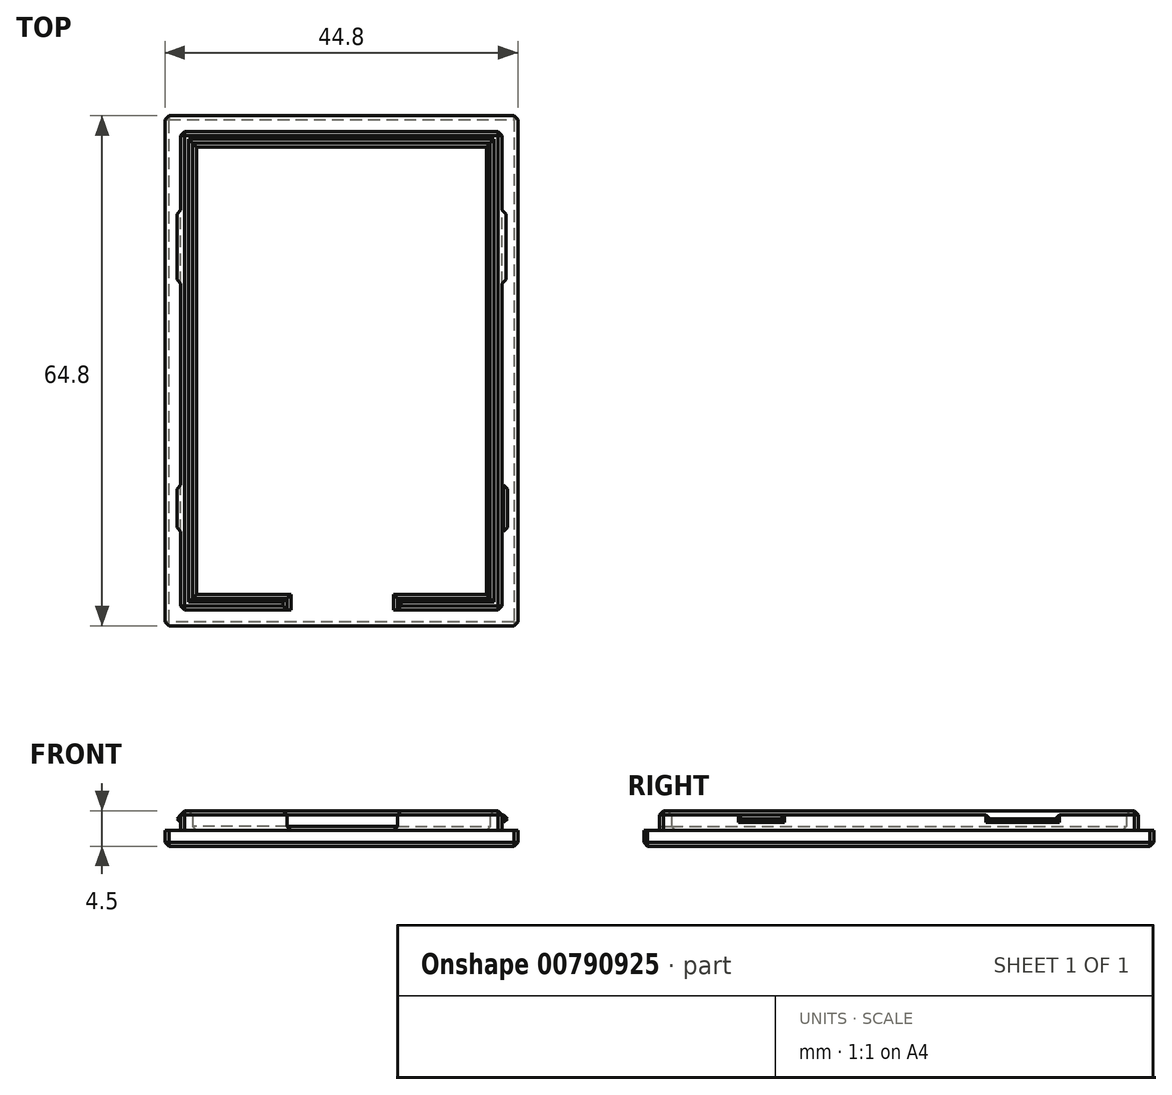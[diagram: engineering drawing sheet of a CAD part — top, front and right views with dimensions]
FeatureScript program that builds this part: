
annotation { "Feature Type Name" : "Feature", "Feature Type Description" : "" }
export const myFeature = defineFeature(function(context is Context, id is Id, definition is map)
    precondition{}
    {
        {
            var Q0;
            Q0=qCreatedBy(makeId("Top.planeOp"),FACE);
            var sketch = newSketch(context, id + "F0", { "sketchPlane" : qUnion([Q0])});
            skLineSegment(sketch, "E0.bottom", {"start": v(-20.5, 35.97) * mm, "end": v(20.3, 35.97) * mm});
            skLineSegment(sketch, "E0.top", {"start": v(-20.5, -24.83) * mm, "end": v(20.3, -24.83) * mm});
            skLineSegment(sketch, "E0.left", {"start": v(-20.5, 35.97) * mm, "end": v(-20.5, -24.83) * mm});
            skLineSegment(sketch, "E0.right", {"start": v(20.3, 35.97) * mm, "end": v(20.3, -24.83) * mm});
            skLineSegment(sketch, "E1.bottom", {"start": v(-22.5, 37.97) * mm, "end": v(22.3, 37.97) * mm});
            skLineSegment(sketch, "E1.top", {"start": v(-22.5, -26.83) * mm, "end": v(22.3, -26.83) * mm});
            skLineSegment(sketch, "E1.left", {"start": v(-22.5, 37.97) * mm, "end": v(-22.5, -26.83) * mm});
            skLineSegment(sketch, "E1.right", {"start": v(22.3, 37.97) * mm, "end": v(22.3, -26.83) * mm});
            skLineSegment(sketch, "E2.bottom", {"start": v(-21, -14.83) * mm, "end": v(21, -14.83) * mm});
            skLineSegment(sketch, "E2.top", {"start": v(-21, -8.96) * mm, "end": v(21, -8.96) * mm});
            skLineSegment(sketch, "E2.left", {"start": v(-21, -14.83) * mm, "end": v(-21, -8.96) * mm});
            skLineSegment(sketch, "E2.right", {"start": v(21, -14.83) * mm, "end": v(21, -8.96) * mm});
            skLineSegment(sketch, "E3.bottom", {"start": v(-21, 16.66) * mm, "end": v(20.8, 16.66) * mm});
            skLineSegment(sketch, "E3.top", {"start": v(-21, 25.97) * mm, "end": v(20.8, 25.97) * mm});
            skLineSegment(sketch, "E3.left", {"start": v(-21, 16.66) * mm, "end": v(-21, 25.97) * mm});
            skLineSegment(sketch, "E3.right", {"start": v(20.8, 16.66) * mm, "end": v(20.8, 25.97) * mm});
            skLineSegment(sketch, "E4.bottom", {"start": v(-17, -29.45) * mm, "end": v(17, -29.45) * mm});
            skLineSegment(sketch, "E4.top", {"start": v(-17, -24.83) * mm, "end": v(17, -24.83) * mm});
            skLineSegment(sketch, "E4.left", {"start": v(-17, -29.45) * mm, "end": v(-17, -24.83) * mm});
            skLineSegment(sketch, "E4.right", {"start": v(17, -29.45) * mm, "end": v(17, -24.83) * mm});
            skLineSegment(sketch, "E5.bottom", {"start": v(-7, -22.91) * mm, "end": v(7, -22.91) * mm});
            skLineSegment(sketch, "E5.top", {"start": v(-7, -32.6) * mm, "end": v(7, -32.6) * mm});
            skLineSegment(sketch, "E5.left", {"start": v(-7, -22.91) * mm, "end": v(-7, -32.6) * mm});
            skLineSegment(sketch, "E5.right", {"start": v(7, -22.91) * mm, "end": v(7, -32.6) * mm});
            skLineSegment(sketch, "E6", {"start": v(22.3, 37.97) * mm, "end": v(27.3, 37.97) * mm});
            skArc(sketch, "E7", {"start": v(27.3, 37.97) * mm, "mid": v(32.3, 32.97) * mm, "end": v(27.3, 27.97) * mm});
            skLineSegment(sketch, "E8", {"start": v(27.3, 27.97) * mm, "end": v(22.3, 25.09) * mm});
            skCircle(sketch, "E9", {"center": v(27.3, 32.97) * mm, "radius": 2.1 * mm});
            skLineSegment(sketch, "E10", {"start": v(-22.5, 37.97) * mm, "end": v(-27.5, 37.97) * mm});
            skArc(sketch, "E11", {"start": v(-27.5, 37.97) * mm, "mid": v(-32.5, 32.97) * mm, "end": v(-27.5, 27.97) * mm});
            skLineSegment(sketch, "E12", {"start": v(-27.5, 27.97) * mm, "end": v(-22.5, 25.09) * mm});
            skLineSegment(sketch, "E13", {"start": v(22.3, -26.83) * mm, "end": v(27.3, -26.83) * mm});
            skArc(sketch, "E14", {"start": v(27.3, -26.83) * mm, "mid": v(32.3, -21.83) * mm, "end": v(27.3, -16.83) * mm});
            skLineSegment(sketch, "E15", {"start": v(27.3, -16.83) * mm, "end": v(22.3, -13.94) * mm});
            skLineSegment(sketch, "E16", {"start": v(-22.5, -26.83) * mm, "end": v(-27.5, -26.83) * mm});
            skArc(sketch, "E17", {"start": v(-27.5, -26.83) * mm, "mid": v(-32.5, -21.83) * mm, "end": v(-27.5, -16.83) * mm});
            skLineSegment(sketch, "E18", {"start": v(-27.5, -16.83) * mm, "end": v(-22.5, -13.94) * mm});
            skCircle(sketch, "E19", {"center": v(-27.5, 32.97) * mm, "radius": 2.1 * mm});
            skCircle(sketch, "E20", {"center": v(-27.5, -21.83) * mm, "radius": 2.1 * mm});
            skCircle(sketch, "E21", {"center": v(27.3, -21.83) * mm, "radius": 2.1 * mm});
            skLineSegment(sketch, "E22.bottom", {"start": v(18.8, 34.47) * mm, "end": v(-19, 34.47) * mm});
            skLineSegment(sketch, "E22.top", {"start": v(18.8, -23.33) * mm, "end": v(-19, -23.33) * mm});
            skLineSegment(sketch, "E22.left", {"start": v(18.8, 34.47) * mm, "end": v(18.8, -23.33) * mm});
            skLineSegment(sketch, "E22.right", {"start": v(-19, 34.47) * mm, "end": v(-19, -23.33) * mm});
            skSolve(sketch);
        }
        {
            var Q0;
            {var subQ29=sQuery(id+"F0.wireOp",EDGE,"E0.bottom");Q0=makeQuery(id+"F0.imprint","IMPRINT",FACE,{"disambiguationData":[TD([[makeQuery(id+"F0.imprint","IMPRINT",EDGE,{"derivedFrom":subQ29}),1.0]])]});}
            var Q1;
            {var subQ29=sQuery(id+"F0.wireOp",EDGE,"E0.bottom");Q1=makeQuery(id+"F0.imprint","IMPRINT",FACE,{"disambiguationData":[TD([[makeQuery(id+"F0.imprint","IMPRINT",EDGE,{"derivedFrom":subQ29}),1.0]])]});}
            var Q2;
            Q2=makeQuery(id+"F0.imprint","IMPRINT",FACE,{"disambiguationData":[TD([[makeQuery(id+"F0.imprint","IMPRINT",EDGE,{"derivedFrom":sQuery(id+"F0.wireOp",EDGE,"677e632e-3eaa-4d09-a5a9-d7e54d0ba1e0")}),-1.0]])]});
            var Q3;
            Q3=makeQuery(id+"F0.imprint","IMPRINT",FACE,{"disambiguationData":[TD([[makeQuery(id+"F0.imprint","IMPRINT",EDGE,{"derivedFrom":sQuery(id+"F0.wireOp",EDGE,"677e632e-3eaa-4d09-a5a9-d7e54d0ba1e0")}),1.0]])]});
            var Q4;
            {var subQ5=sQuery(id+"F0.wireOp",EDGE,"E0.bottom");Q4=makeQuery(id+"F0.imprint","IMPRINT",FACE,{"disambiguationData":[TD([[makeQuery(id+"F0.imprint","IMPRINT",EDGE,{"derivedFrom":subQ5}),-1.0]])]});}
            var Q5;
            Q5=makeQuery(id+"F0.imprint","IMPRINT",FACE,{"disambiguationData":[TD([[makeQuery(id+"F0.imprint","IMPRINT",EDGE,{"derivedFrom":sQuery(id+"F0.wireOp",EDGE,"480dd3ae-46e1-4b28-823d-24966efe9ffa")}),-1.0]])]});
            var Q6;
            Q6=makeQuery(id+"F0.imprint","IMPRINT",FACE,{"disambiguationData":[TD([[makeQuery(id+"F0.imprint","IMPRINT",EDGE,{"derivedFrom":sQuery(id+"F0.wireOp",EDGE,"480dd3ae-46e1-4b28-823d-24966efe9ffa")}),1.0]])]});
            var Q7;
            {var subQ29=sQuery(id+"F0.wireOp",EDGE,"E0.bottom");Q7=makeQuery(id+"F0.imprint","IMPRINT",FACE,{"disambiguationData":[TD([[makeQuery(id+"F0.imprint","IMPRINT",EDGE,{"derivedFrom":subQ29}),1.0]])]});}
            var Q8;
            {var subQ0=sQuery(id+"F0.wireOp",EDGE,"E3.bottom");var subQ1=sQuery(id+"F0.wireOp",EDGE,"E0.left");var subQ2=makeQuery(id+"F0.imprint","INTERSECT",VERTEX,{"derivedFrom":[subQ1,subQ0]});Q8=makeQuery(id+"F0.imprint","IMPRINT",FACE,{"disambiguationData":[TD([[makeQuery(id+"F0.imprint","IMPRINT",EDGE,{"disambiguationData":[TD([[subQ2,1.0]])],"derivedFrom":subQ1}),1.0]])]});}
            var Q9;
            {var subQ0=sQuery(id+"F0.wireOp",EDGE,"E3.bottom");var subQ1=sQuery(id+"F0.wireOp",EDGE,"E0.left");var subQ2=makeQuery(id+"F0.imprint","INTERSECT",VERTEX,{"derivedFrom":[subQ1,subQ0]});Q9=makeQuery(id+"F0.imprint","IMPRINT",FACE,{"disambiguationData":[TD([[makeQuery(id+"F0.imprint","IMPRINT",EDGE,{"disambiguationData":[TD([[subQ2,-1.0]])],"derivedFrom":subQ1}),1.0]])]});}
            var Q10;
            {var subQ3=sQuery(id+"F0.wireOp",EDGE,"1f75b855-5066-40c4-a874-72f5a5b6cba5");var subQ5=sQuery(id+"F0.wireOp",EDGE,"E4.top");var subQ6=makeQuery(id+"F0.imprint","INTERSECT",VERTEX,{"derivedFrom":[subQ3,subQ5]});Q10=makeQuery(id+"F0.imprint","IMPRINT",FACE,{"disambiguationData":[TD([[makeQuery(id+"F0.imprint","IMPRINT",EDGE,{"disambiguationData":[TD([[subQ6,-1.0]])],"derivedFrom":subQ3}),-1.0]])]});}
            var Q11;
            Q11=makeQuery(id+"F0.imprint","IMPRINT",FACE,{"disambiguationData":[TD([[makeQuery(id+"F0.imprint","IMPRINT",EDGE,{"derivedFrom":sQuery(id+"F0.wireOp",EDGE,"79218117-f56a-448c-9f48-c8c58d9f12d9")}),-1.0]])]});
            var Q12;
            {var subQ29=sQuery(id+"F0.wireOp",EDGE,"E0.bottom");Q12=makeQuery(id+"F0.imprint","IMPRINT",FACE,{"disambiguationData":[TD([[makeQuery(id+"F0.imprint","IMPRINT",EDGE,{"derivedFrom":subQ29}),1.0]])]});}
            var Q13;
            {var subQ1=sQuery(id+"F0.wireOp",EDGE,"E5.bottom");Q13=makeQuery(id+"F0.imprint","IMPRINT",FACE,{"disambiguationData":[TD([[makeQuery(id+"F0.imprint","IMPRINT",EDGE,{"derivedFrom":subQ1}),1.0]])]});}
            var Q14;
            {var subQ0=sQuery(id+"F0.wireOp",EDGE,"E2.bottom");var subQ1=sQuery(id+"F0.wireOp",EDGE,"E0.left");var subQ2=makeQuery(id+"F0.imprint","INTERSECT",VERTEX,{"derivedFrom":[subQ1,subQ0]});Q14=makeQuery(id+"F0.imprint","IMPRINT",FACE,{"disambiguationData":[TD([[makeQuery(id+"F0.imprint","IMPRINT",EDGE,{"disambiguationData":[TD([[subQ2,1.0]])],"derivedFrom":subQ1}),1.0]])]});}
            var Q15;
            Q15=makeQuery(id+"F0.imprint","IMPRINT",FACE,{"disambiguationData":[TD([[makeQuery(id+"F0.imprint","IMPRINT",EDGE,{"derivedFrom":sQuery(id+"F0.wireOp",EDGE,"ba33dbd0-b231-4e40-89bf-cbb7f6c2f6bb")}),-1.0]])]});
            var Q16;
            {var subQ0=sQuery(id+"F0.wireOp",EDGE,"E4.left");var subQ3=sQuery(id+"F0.wireOp",EDGE,"849d3ca8-0fda-44a0-b916-5b7dc914c84e");var subQ4=makeQuery(id+"F0.imprint","INTERSECT",VERTEX,{"derivedFrom":[subQ3,subQ0]});Q16=makeQuery(id+"F0.imprint","IMPRINT",FACE,{"disambiguationData":[TD([[makeQuery(id+"F0.imprint","IMPRINT",EDGE,{"disambiguationData":[TD([[subQ4,-1.0]])],"derivedFrom":subQ3}),-1.0]])]});}
            var Q17;
            {var subQ0=sQuery(id+"F0.wireOp",EDGE,"E5.left");var subQ1=sQuery(id+"F0.wireOp",EDGE,"E0.top");var subQ2=makeQuery(id+"F0.imprint","INTERSECT",VERTEX,{"derivedFrom":[subQ1,subQ0]});Q17=makeQuery(id+"F0.imprint","IMPRINT",FACE,{"disambiguationData":[TD([[makeQuery(id+"F0.imprint","IMPRINT",EDGE,{"disambiguationData":[TD([[subQ2,-1.0]])],"derivedFrom":subQ1}),-1.0]])]});}
            var Q18;
            {var subQ0=sQuery(id+"F0.wireOp",EDGE,"E5.bottom");Q18=makeQuery(id+"F0.imprint","IMPRINT",FACE,{"disambiguationData":[TD([[makeQuery(id+"F0.imprint","IMPRINT",EDGE,{"derivedFrom":subQ0}),-1.0]])]});}
            var Q19;
            Q19=makeQuery(id+"F0.imprint","IMPRINT",FACE,{"disambiguationData":[TD([[makeQuery(id+"F0.imprint","IMPRINT",EDGE,{"derivedFrom":sQuery(id+"F0.wireOp",EDGE,"ba33dbd0-b231-4e40-89bf-cbb7f6c2f6bb")}),1.0]])]});
            var Q20;
            {var subQ29=sQuery(id+"F0.wireOp",EDGE,"E0.bottom");Q20=makeQuery(id+"F0.imprint","IMPRINT",FACE,{"disambiguationData":[TD([[makeQuery(id+"F0.imprint","IMPRINT",EDGE,{"derivedFrom":subQ29}),1.0]])]});}
            var Q21;
            {var subQ1=sQuery(id+"F0.wireOp",EDGE,"E0.top");var subQ3=sQuery(id+"F0.wireOp",EDGE,"849d3ca8-0fda-44a0-b916-5b7dc914c84e");var subQ4=makeQuery(id+"F0.imprint","INTERSECT",VERTEX,{"derivedFrom":[subQ1,subQ3]});Q21=makeQuery(id+"F0.imprint","IMPRINT",FACE,{"disambiguationData":[TD([[makeQuery(id+"F0.imprint","IMPRINT",EDGE,{"disambiguationData":[TD([[subQ4,-1.0]])],"derivedFrom":subQ3}),1.0]])]});}
            var Q22;
            {var subQ5=sQuery(id+"F0.wireOp",EDGE,"E0.top");var subQ8=sQuery(id+"F0.wireOp",EDGE,"E5.left");var subQ9=makeQuery(id+"F0.imprint","INTERSECT",VERTEX,{"derivedFrom":[subQ5,subQ8]});Q22=makeQuery(id+"F0.imprint","IMPRINT",FACE,{"disambiguationData":[TD([[makeQuery(id+"F0.imprint","IMPRINT",EDGE,{"disambiguationData":[TD([[subQ9,1.0]])],"derivedFrom":subQ5}),1.0]])]});}
            var Q23;
            {var subQ0=sQuery(id+"F0.wireOp",EDGE,"E4.left");var subQ1=sQuery(id+"F0.wireOp",EDGE,"849d3ca8-0fda-44a0-b916-5b7dc914c84e");var subQ2=makeQuery(id+"F0.imprint","INTERSECT",VERTEX,{"derivedFrom":[subQ1,subQ0]});Q23=makeQuery(id+"F0.imprint","IMPRINT",FACE,{"disambiguationData":[TD([[makeQuery(id+"F0.imprint","IMPRINT",EDGE,{"disambiguationData":[TD([[subQ2,-1.0]])],"derivedFrom":subQ1}),1.0]])]});}
            var Q24;
            {var subQ0=sQuery(id+"F0.wireOp",EDGE,"E4.top");var subQ1=sQuery(id+"F0.wireOp",EDGE,"1f75b855-5066-40c4-a874-72f5a5b6cba5");var subQ2=makeQuery(id+"F0.imprint","INTERSECT",VERTEX,{"derivedFrom":[subQ1,subQ0]});Q24=makeQuery(id+"F0.imprint","IMPRINT",FACE,{"disambiguationData":[TD([[makeQuery(id+"F0.imprint","IMPRINT",EDGE,{"disambiguationData":[TD([[subQ2,-1.0]])],"derivedFrom":subQ1}),1.0]])]});}
            var Q25;
            {var subQ0=sQuery(id+"F0.wireOp",EDGE,"1f75b855-5066-40c4-a874-72f5a5b6cba5");var subQ3=sQuery(id+"F0.wireOp",EDGE,"E4.right");var subQ5=makeQuery(id+"F0.imprint","INTERSECT",VERTEX,{"derivedFrom":[subQ0,subQ3]});Q25=makeQuery(id+"F0.imprint","IMPRINT",FACE,{"disambiguationData":[TD([[makeQuery(id+"F0.imprint","IMPRINT",EDGE,{"disambiguationData":[TD([[subQ5,-1.0]])],"derivedFrom":subQ0}),1.0]])]});}
            var Q26;
            Q26=makeQuery(id+"F0.imprint","IMPRINT",FACE,{"disambiguationData":[TD([[makeQuery(id+"F0.imprint","IMPRINT",EDGE,{"derivedFrom":sQuery(id+"F0.wireOp",EDGE,"79218117-f56a-448c-9f48-c8c58d9f12d9")}),1.0]])]});
            var Q27;
            {var subQ5=sQuery(id+"F0.wireOp",EDGE,"E2.right");Q27=makeQuery(id+"F0.imprint","IMPRINT",FACE,{"disambiguationData":[TD([[makeQuery(id+"F0.imprint","IMPRINT",EDGE,{"derivedFrom":subQ5}),1.0]])]});}
            var Q28;
            {var subQ5=sQuery(id+"F0.wireOp",EDGE,"E2.left");Q28=makeQuery(id+"F0.imprint","IMPRINT",FACE,{"disambiguationData":[TD([[makeQuery(id+"F0.imprint","IMPRINT",EDGE,{"derivedFrom":subQ5}),-1.0]])]});}
            var Q29;
            {var subQ5=sQuery(id+"F0.wireOp",EDGE,"E3.left");Q29=makeQuery(id+"F0.imprint","IMPRINT",FACE,{"disambiguationData":[TD([[makeQuery(id+"F0.imprint","IMPRINT",EDGE,{"derivedFrom":subQ5}),-1.0]])]});}
            var Q30;
            {var subQ5=sQuery(id+"F0.wireOp",EDGE,"E3.right");Q30=makeQuery(id+"F0.imprint","IMPRINT",FACE,{"disambiguationData":[TD([[makeQuery(id+"F0.imprint","IMPRINT",EDGE,{"derivedFrom":subQ5}),1.0]])]});}
            var Q31;
            {var subQ5=sQuery(id+"F0.wireOp",EDGE,"E22.bottom");Q31=makeQuery(id+"F0.imprint","IMPRINT",FACE,{"disambiguationData":[TD([[makeQuery(id+"F0.imprint","IMPRINT",EDGE,{"derivedFrom":subQ5}),1.0]])]});}
            var Q32;
            {var subQ0=sQuery(id+"F0.wireOp",EDGE,"E22.right");var subQ1=sQuery(id+"F0.wireOp",EDGE,"E3.bottom");var subQ2=makeQuery(id+"F0.imprint","INTERSECT",VERTEX,{"derivedFrom":[subQ1,subQ0]});Q32=makeQuery(id+"F0.imprint","IMPRINT",FACE,{"disambiguationData":[TD([[makeQuery(id+"F0.imprint","IMPRINT",EDGE,{"disambiguationData":[TD([[subQ2,-1.0]])],"derivedFrom":subQ1}),1.0]])]});}
            var Q33;
            {var subQ0=sQuery(id+"F0.wireOp",EDGE,"E22.right");var subQ1=sQuery(id+"F0.wireOp",EDGE,"E2.top");var subQ2=makeQuery(id+"F0.imprint","INTERSECT",VERTEX,{"derivedFrom":[subQ1,subQ0]});Q33=makeQuery(id+"F0.imprint","IMPRINT",FACE,{"disambiguationData":[TD([[makeQuery(id+"F0.imprint","IMPRINT",EDGE,{"disambiguationData":[TD([[subQ2,-1.0]])],"derivedFrom":subQ1}),1.0]])]});}
            var Q34;
            {var subQ0=sQuery(id+"F0.wireOp",EDGE,"E22.right");var subQ1=sQuery(id+"F0.wireOp",EDGE,"E2.bottom");var subQ2=makeQuery(id+"F0.imprint","INTERSECT",VERTEX,{"derivedFrom":[subQ1,subQ0]});Q34=makeQuery(id+"F0.imprint","IMPRINT",FACE,{"disambiguationData":[TD([[makeQuery(id+"F0.imprint","IMPRINT",EDGE,{"disambiguationData":[TD([[subQ2,-1.0]])],"derivedFrom":subQ1}),1.0]])]});}
            var Q35;
            {var subQ0=sQuery(id+"F0.wireOp",EDGE,"E5.left");var subQ1=sQuery(id+"F0.wireOp",EDGE,"E0.top");var subQ2=makeQuery(id+"F0.imprint","INTERSECT",VERTEX,{"derivedFrom":[subQ1,subQ0]});Q35=makeQuery(id+"F0.imprint","IMPRINT",FACE,{"disambiguationData":[TD([[makeQuery(id+"F0.imprint","IMPRINT",EDGE,{"disambiguationData":[TD([[subQ2,1.0]])],"derivedFrom":subQ1}),-1.0]])]});}
            var Q36;
            {var subQ0=sQuery(id+"F0.wireOp",EDGE,"E5.left");var subQ1=sQuery(id+"F0.wireOp",EDGE,"E0.top");var subQ2=makeQuery(id+"F0.imprint","INTERSECT",VERTEX,{"derivedFrom":[subQ1,subQ0]});Q36=makeQuery(id+"F0.imprint","IMPRINT",FACE,{"disambiguationData":[TD([[makeQuery(id+"F0.imprint","IMPRINT",EDGE,{"disambiguationData":[TD([[subQ2,-1.0]])],"derivedFrom":subQ1}),1.0]])]});}
            var Q37;
            {var subQ5=sQuery(id+"F0.wireOp",EDGE,"E0.top");var subQ7=makeQuery(id+"F0.imprint","INTERSECT",VERTEX,{"derivedFrom":[subQ5,sQuery(id+"F0.wireOp",EDGE,"E4.right")]});Q37=makeQuery(id+"F0.imprint","IMPRINT",FACE,{"disambiguationData":[TD([[makeQuery(id+"F0.imprint","IMPRINT",EDGE,{"disambiguationData":[TD([[subQ7,1.0]])],"derivedFrom":subQ5}),1.0]])]});}
            var Q38;
            {var subQ0=sQuery(id+"F0.wireOp",EDGE,"E4.right");var subQ1=sQuery(id+"F0.wireOp",EDGE,"E0.top");var subQ2=makeQuery(id+"F0.imprint","INTERSECT",VERTEX,{"derivedFrom":[subQ1,subQ0]});Q38=makeQuery(id+"F0.imprint","IMPRINT",FACE,{"disambiguationData":[TD([[makeQuery(id+"F0.imprint","IMPRINT",EDGE,{"disambiguationData":[TD([[subQ2,1.0]])],"derivedFrom":subQ1}),-1.0]])]});}
            var Q39;
            {var subQ0=sQuery(id+"F0.wireOp",EDGE,"E2.bottom");var subQ1=sQuery(id+"F0.wireOp",EDGE,"E0.right");var subQ2=makeQuery(id+"F0.imprint","INTERSECT",VERTEX,{"derivedFrom":[subQ1,subQ0]});Q39=makeQuery(id+"F0.imprint","IMPRINT",FACE,{"disambiguationData":[TD([[makeQuery(id+"F0.imprint","IMPRINT",EDGE,{"disambiguationData":[TD([[subQ2,1.0]])],"derivedFrom":subQ1}),-1.0]])]});}
            var Q40;
            {var subQ0=sQuery(id+"F0.wireOp",EDGE,"E3.bottom");var subQ1=sQuery(id+"F0.wireOp",EDGE,"E0.right");var subQ2=makeQuery(id+"F0.imprint","INTERSECT",VERTEX,{"derivedFrom":[subQ1,subQ0]});Q40=makeQuery(id+"F0.imprint","IMPRINT",FACE,{"disambiguationData":[TD([[makeQuery(id+"F0.imprint","IMPRINT",EDGE,{"disambiguationData":[TD([[subQ2,-1.0]])],"derivedFrom":subQ1}),-1.0]])]});}
            var Q41;
            {var subQ0=sQuery(id+"F0.wireOp",EDGE,"E3.bottom");var subQ1=sQuery(id+"F0.wireOp",EDGE,"E0.right");var subQ2=makeQuery(id+"F0.imprint","INTERSECT",VERTEX,{"derivedFrom":[subQ1,subQ0]});Q41=makeQuery(id+"F0.imprint","IMPRINT",FACE,{"disambiguationData":[TD([[makeQuery(id+"F0.imprint","IMPRINT",EDGE,{"disambiguationData":[TD([[subQ2,1.0]])],"derivedFrom":subQ1}),-1.0]])]});}
            extrude(context, id + "F1", {"entities" : qUnion([Q0, Q1, Q2, Q3, Q4, Q5, Q6, Q7, Q8, Q9, Q10, Q11, Q12, Q13, Q14, Q15, Q16, Q17, Q18, Q19, Q20, Q21, Q22, Q23, Q24, Q25, Q26, Q27, Q28, Q29, Q30, Q31, Q32, Q33, Q34, Q35, Q36, Q37, Q38, Q39, Q40, Q41]), "depth" : 2 * mm, "offsetDistance" : 25 * mm});
        }
        {
            var Q0;
            {var subQ5=sQuery(id+"F0.wireOp",EDGE,"E0.bottom");Q0=makeQuery(id+"F0.imprint","IMPRINT",FACE,{"disambiguationData":[TD([[makeQuery(id+"F0.imprint","IMPRINT",EDGE,{"derivedFrom":subQ5}),-1.0]])]});}
            var Q1;
            {var subQ0=sQuery(id+"F0.wireOp",EDGE,"E3.bottom");var subQ1=sQuery(id+"F0.wireOp",EDGE,"E0.left");var subQ2=makeQuery(id+"F0.imprint","INTERSECT",VERTEX,{"derivedFrom":[subQ1,subQ0]});Q1=makeQuery(id+"F0.imprint","IMPRINT",FACE,{"disambiguationData":[TD([[makeQuery(id+"F0.imprint","IMPRINT",EDGE,{"disambiguationData":[TD([[subQ2,1.0]])],"derivedFrom":subQ1}),1.0]])]});}
            var Q2;
            {var subQ0=sQuery(id+"F0.wireOp",EDGE,"E3.bottom");var subQ1=sQuery(id+"F0.wireOp",EDGE,"E0.left");var subQ2=makeQuery(id+"F0.imprint","INTERSECT",VERTEX,{"derivedFrom":[subQ1,subQ0]});Q2=makeQuery(id+"F0.imprint","IMPRINT",FACE,{"disambiguationData":[TD([[makeQuery(id+"F0.imprint","IMPRINT",EDGE,{"disambiguationData":[TD([[subQ2,-1.0]])],"derivedFrom":subQ1}),1.0]])]});}
            var Q3;
            {var subQ0=sQuery(id+"F0.wireOp",EDGE,"E3.bottom");var subQ1=sQuery(id+"F0.wireOp",EDGE,"E0.right");var subQ2=makeQuery(id+"F0.imprint","INTERSECT",VERTEX,{"derivedFrom":[subQ1,subQ0]});Q3=makeQuery(id+"F0.imprint","IMPRINT",FACE,{"disambiguationData":[TD([[makeQuery(id+"F0.imprint","IMPRINT",EDGE,{"disambiguationData":[TD([[subQ2,1.0]])],"derivedFrom":subQ1}),-1.0]])]});}
            var Q4;
            {var subQ0=sQuery(id+"F0.wireOp",EDGE,"E3.bottom");var subQ1=sQuery(id+"F0.wireOp",EDGE,"E0.right");var subQ2=makeQuery(id+"F0.imprint","INTERSECT",VERTEX,{"derivedFrom":[subQ1,subQ0]});Q4=makeQuery(id+"F0.imprint","IMPRINT",FACE,{"disambiguationData":[TD([[makeQuery(id+"F0.imprint","IMPRINT",EDGE,{"disambiguationData":[TD([[subQ2,-1.0]])],"derivedFrom":subQ1}),-1.0]])]});}
            var Q5;
            {var subQ5=sQuery(id+"F0.wireOp",EDGE,"E0.top");var subQ7=makeQuery(id+"F0.imprint","INTERSECT",VERTEX,{"derivedFrom":[subQ5,sQuery(id+"F0.wireOp",EDGE,"E4.right")]});Q5=makeQuery(id+"F0.imprint","IMPRINT",FACE,{"disambiguationData":[TD([[makeQuery(id+"F0.imprint","IMPRINT",EDGE,{"disambiguationData":[TD([[subQ7,1.0]])],"derivedFrom":subQ5}),1.0]])]});}
            var Q6;
            {var subQ0=sQuery(id+"F0.wireOp",EDGE,"E2.bottom");var subQ1=sQuery(id+"F0.wireOp",EDGE,"E0.right");var subQ2=makeQuery(id+"F0.imprint","INTERSECT",VERTEX,{"derivedFrom":[subQ1,subQ0]});Q6=makeQuery(id+"F0.imprint","IMPRINT",FACE,{"disambiguationData":[TD([[makeQuery(id+"F0.imprint","IMPRINT",EDGE,{"disambiguationData":[TD([[subQ2,1.0]])],"derivedFrom":subQ1}),-1.0]])]});}
            var Q7;
            {var subQ5=sQuery(id+"F0.wireOp",EDGE,"E0.top");var subQ8=sQuery(id+"F0.wireOp",EDGE,"E5.left");var subQ9=makeQuery(id+"F0.imprint","INTERSECT",VERTEX,{"derivedFrom":[subQ5,subQ8]});Q7=makeQuery(id+"F0.imprint","IMPRINT",FACE,{"disambiguationData":[TD([[makeQuery(id+"F0.imprint","IMPRINT",EDGE,{"disambiguationData":[TD([[subQ9,1.0]])],"derivedFrom":subQ5}),1.0]])]});}
            var Q8;
            {var subQ0=sQuery(id+"F0.wireOp",EDGE,"E2.bottom");var subQ1=sQuery(id+"F0.wireOp",EDGE,"E0.left");var subQ2=makeQuery(id+"F0.imprint","INTERSECT",VERTEX,{"derivedFrom":[subQ1,subQ0]});Q8=makeQuery(id+"F0.imprint","IMPRINT",FACE,{"disambiguationData":[TD([[makeQuery(id+"F0.imprint","IMPRINT",EDGE,{"disambiguationData":[TD([[subQ2,1.0]])],"derivedFrom":subQ1}),1.0]])]});}
            extrude(context, id + "F2", {"entities" : qUnion([Q0, Q1, Q2, Q3, Q4, Q5, Q6, Q7, Q8]), "operationType" : NewBodyOperationType.ADD, "depth" : 4.5 * mm, "offsetDistance" : 25 * mm, "hasSecondDirection" : true, "secondDirectionOppositeDirection" : false, "secondDirectionDepth" : 1 * mm});
        }
        {
            var Q0;
            {var subQ5=sQuery(id+"F0.wireOp",EDGE,"E3.right");Q0=makeQuery(id+"F0.imprint","IMPRINT",FACE,{"disambiguationData":[TD([[makeQuery(id+"F0.imprint","IMPRINT",EDGE,{"derivedFrom":subQ5}),1.0]])]});}
            var Q1;
            {var subQ5=sQuery(id+"F0.wireOp",EDGE,"E3.left");Q1=makeQuery(id+"F0.imprint","IMPRINT",FACE,{"disambiguationData":[TD([[makeQuery(id+"F0.imprint","IMPRINT",EDGE,{"derivedFrom":subQ5}),-1.0]])]});}
            var Q2;
            {var subQ5=sQuery(id+"F0.wireOp",EDGE,"E2.left");Q2=makeQuery(id+"F0.imprint","IMPRINT",FACE,{"disambiguationData":[TD([[makeQuery(id+"F0.imprint","IMPRINT",EDGE,{"derivedFrom":subQ5}),-1.0]])]});}
            var Q3;
            {var subQ5=sQuery(id+"F0.wireOp",EDGE,"E2.right");Q3=makeQuery(id+"F0.imprint","IMPRINT",FACE,{"disambiguationData":[TD([[makeQuery(id+"F0.imprint","IMPRINT",EDGE,{"derivedFrom":subQ5}),1.0]])]});}
            extrude(context, id + "F3", {"entities" : qUnion([Q0, Q1, Q2, Q3]), "operationType" : NewBodyOperationType.ADD, "depth" : 4 * mm, "offsetDistance" : 25 * mm, "hasSecondDirection" : true, "secondDirectionOppositeDirection" : false, "secondDirectionDepth" : 3 * mm});
        }
        {
            var Q0;
            Q0=makeQuery(id+"F3.opExtrude","SWEPT_FACE",FACE,{"disambiguationData":[OSD([sQuery(id+"F0.wireOp",EDGE,"E3.left")])]});
            var Q1;
            Q1=makeQuery(id+"F3.opExtrude","SWEPT_FACE",FACE,{"disambiguationData":[OSD([sQuery(id+"F0.wireOp",EDGE,"E2.left")])]});
            var Q2;
            Q2=makeQuery(id+"F3.opExtrude","SWEPT_FACE",FACE,{"disambiguationData":[OSD([sQuery(id+"F0.wireOp",EDGE,"E3.right")])]});
            var Q3;
            Q3=makeQuery(id+"F3.opExtrude","SWEPT_FACE",FACE,{"disambiguationData":[OSD([sQuery(id+"F0.wireOp",EDGE,"E2.right")])]});
            var Q4;
            Q4=makeQuery(id+"F2.opExtrude","SWEPT_EDGE",EDGE,{"disambiguationData":[OSD([sQuery(id+"F0.wireOp",EDGE,"E0.top"),sQuery(id+"F0.wireOp",EDGE,"E0.right")])]});
            var Q5;
            Q5=makeQuery(id+"F2.opExtrude","SWEPT_EDGE",EDGE,{"disambiguationData":[OSD([sQuery(id+"F0.wireOp",EDGE,"E0.bottom"),sQuery(id+"F0.wireOp",EDGE,"E0.right")])]});
            var Q6;
            Q6=makeQuery(id+"F2.opExtrude","CAP_FACE",FACE,{"disambiguationData":[OSD([sQuery(id+"F0.wireOp",EDGE,"E0.bottom"),sQuery(id+"F0.wireOp",EDGE,"E0.top"),sQuery(id+"F0.wireOp",EDGE,"E0.left"),sQuery(id+"F0.wireOp",EDGE,"E0.right"),sQuery(id+"F0.wireOp",EDGE,"E5.left"),sQuery(id+"F0.wireOp",EDGE,"E5.right"),sQuery(id+"F0.wireOp",EDGE,"E22.bottom"),sQuery(id+"F0.wireOp",EDGE,"E22.top"),sQuery(id+"F0.wireOp",EDGE,"E22.left"),sQuery(id+"F0.wireOp",EDGE,"E22.right")])],"isStart":false});
            var Q7;
            Q7=makeQuery(id+"F2.opExtrude","SWEPT_EDGE",EDGE,{"disambiguationData":[OSD([sQuery(id+"F0.wireOp",EDGE,"E0.bottom"),sQuery(id+"F0.wireOp",EDGE,"E0.left")])]});
            var Q8;
            Q8=makeQuery(id+"F1.opExtrude","SWEPT_EDGE",EDGE,{"disambiguationData":[OSD([sQuery(id+"F0.wireOp",EDGE,"E1.bottom"),sQuery(id+"F0.wireOp",EDGE,"E1.left"),sQuery(id+"F0.wireOp",EDGE,"E10")])]});
            var Q9;
            Q9=makeQuery(id+"F2.opExtrude","SWEPT_EDGE",EDGE,{"disambiguationData":[OSD([sQuery(id+"F0.wireOp",EDGE,"E0.top"),sQuery(id+"F0.wireOp",EDGE,"E0.left")])]});
            var Q10;
            Q10=makeQuery(id+"F1.opExtrude","SWEPT_EDGE",EDGE,{"disambiguationData":[OSD([sQuery(id+"F0.wireOp",EDGE,"E1.top"),sQuery(id+"F0.wireOp",EDGE,"E1.left"),sQuery(id+"F0.wireOp",EDGE,"E16")])]});
            var Q11;
            Q11=makeQuery(id+"F1.opExtrude","SWEPT_EDGE",EDGE,{"disambiguationData":[OSD([sQuery(id+"F0.wireOp",EDGE,"E1.top"),sQuery(id+"F0.wireOp",EDGE,"E1.right"),sQuery(id+"F0.wireOp",EDGE,"E13")])]});
            var Q12;
            Q12=makeQuery(id+"F1.opExtrude","CAP_FACE",FACE,{"disambiguationData":[OSD([sQuery(id+"F0.wireOp",EDGE,"E1.bottom"),sQuery(id+"F0.wireOp",EDGE,"E1.top"),sQuery(id+"F0.wireOp",EDGE,"E1.left"),sQuery(id+"F0.wireOp",EDGE,"E1.right")])],"isStart":true});
            var Q13;
            {var subQ0=sQuery(id+"F0.wireOp",EDGE,"E22.top");Q13=makeQuery(id+"F2.boolean.opBoolean","INTERSECT",EDGE,{"derivedFrom":[makeQuery(id+"F1.opExtrude","CAP_FACE",FACE,{"disambiguationData":[OSD([sQuery(id+"F0.wireOp",EDGE,"E1.bottom"),sQuery(id+"F0.wireOp",EDGE,"E1.top"),sQuery(id+"F0.wireOp",EDGE,"E1.left"),sQuery(id+"F0.wireOp",EDGE,"E1.right")])],"isStart":false}),makeQuery(id+"F2.opExtrude","SWEPT_FACE",FACE,{"disambiguationData":[OSD([subQ0]),TDD([makeQuery(id+"F0.imprint","IMPRINT",EDGE,{"disambiguationData":[TD([[makeQuery(id+"F0.imprint","INTERSECT",VERTEX,{"derivedFrom":[sQuery(id+"F0.wireOp",EDGE,"E5.right"),subQ0]}),1.0]])],"derivedFrom":subQ0})])]})]});}
            var Q14;
            Q14=makeQuery(id+"F2.boolean.opBoolean","INTERSECT",EDGE,{"derivedFrom":[makeQuery(id+"F1.opExtrude","CAP_FACE",FACE,{"disambiguationData":[OSD([sQuery(id+"F0.wireOp",EDGE,"E1.bottom"),sQuery(id+"F0.wireOp",EDGE,"E1.top"),sQuery(id+"F0.wireOp",EDGE,"E1.left"),sQuery(id+"F0.wireOp",EDGE,"E1.right")])],"isStart":false}),makeQuery(id+"F2.opExtrude","SWEPT_FACE",FACE,{"disambiguationData":[OSD([sQuery(id+"F0.wireOp",EDGE,"E22.left")])]})]});
            var Q15;
            {var subQ0=sQuery(id+"F0.wireOp",EDGE,"E22.top");Q15=makeQuery(id+"F2.boolean.opBoolean","INTERSECT",EDGE,{"derivedFrom":[makeQuery(id+"F1.opExtrude","CAP_FACE",FACE,{"disambiguationData":[OSD([sQuery(id+"F0.wireOp",EDGE,"E1.bottom"),sQuery(id+"F0.wireOp",EDGE,"E1.top"),sQuery(id+"F0.wireOp",EDGE,"E1.left"),sQuery(id+"F0.wireOp",EDGE,"E1.right")])],"isStart":false}),makeQuery(id+"F2.opExtrude","SWEPT_FACE",FACE,{"disambiguationData":[OSD([subQ0]),TDD([makeQuery(id+"F0.imprint","IMPRINT",EDGE,{"disambiguationData":[TD([[makeQuery(id+"F0.imprint","INTERSECT",VERTEX,{"derivedFrom":[sQuery(id+"F0.wireOp",EDGE,"E5.left"),subQ0]}),-1.0]])],"derivedFrom":subQ0})])]})]});}
            var Q16;
            Q16=makeQuery(id+"F2.boolean.opBoolean","INTERSECT",EDGE,{"derivedFrom":[makeQuery(id+"F1.opExtrude","CAP_FACE",FACE,{"disambiguationData":[OSD([sQuery(id+"F0.wireOp",EDGE,"E1.bottom"),sQuery(id+"F0.wireOp",EDGE,"E1.top"),sQuery(id+"F0.wireOp",EDGE,"E1.left"),sQuery(id+"F0.wireOp",EDGE,"E1.right")])],"isStart":false}),makeQuery(id+"F2.opExtrude","SWEPT_FACE",FACE,{"disambiguationData":[OSD([sQuery(id+"F0.wireOp",EDGE,"E22.right")])]})]});
            var Q17;
            Q17=makeQuery(id+"F2.boolean.opBoolean","INTERSECT",EDGE,{"derivedFrom":[makeQuery(id+"F1.opExtrude","CAP_FACE",FACE,{"disambiguationData":[OSD([sQuery(id+"F0.wireOp",EDGE,"E1.bottom"),sQuery(id+"F0.wireOp",EDGE,"E1.top"),sQuery(id+"F0.wireOp",EDGE,"E1.left"),sQuery(id+"F0.wireOp",EDGE,"E1.right")])],"isStart":false}),makeQuery(id+"F2.opExtrude","SWEPT_FACE",FACE,{"disambiguationData":[OSD([sQuery(id+"F0.wireOp",EDGE,"E22.bottom")])]})]});
            var Q18;
            Q18=makeQuery(id+"F2.boolean.opBoolean","INTERSECT",EDGE,{"derivedFrom":[makeQuery(id+"F1.opExtrude","CAP_FACE",FACE,{"disambiguationData":[OSD([sQuery(id+"F0.wireOp",EDGE,"E1.bottom"),sQuery(id+"F0.wireOp",EDGE,"E1.top"),sQuery(id+"F0.wireOp",EDGE,"E1.left"),sQuery(id+"F0.wireOp",EDGE,"E1.right")])],"isStart":false}),makeQuery(id+"F2.opExtrude","SWEPT_FACE",FACE,{"disambiguationData":[OSD([sQuery(id+"F0.wireOp",EDGE,"E5.right")])]})]});
            var Q19;
            Q19=makeQuery(id+"F2.boolean.opBoolean","INTERSECT",EDGE,{"derivedFrom":[makeQuery(id+"F1.opExtrude","CAP_FACE",FACE,{"disambiguationData":[OSD([sQuery(id+"F0.wireOp",EDGE,"E1.bottom"),sQuery(id+"F0.wireOp",EDGE,"E1.top"),sQuery(id+"F0.wireOp",EDGE,"E1.left"),sQuery(id+"F0.wireOp",EDGE,"E1.right")])],"isStart":false}),makeQuery(id+"F2.opExtrude","SWEPT_FACE",FACE,{"disambiguationData":[OSD([sQuery(id+"F0.wireOp",EDGE,"E5.left")])]})]});
            var Q20;
            Q20=makeQuery(id+"F1.opExtrude","SWEPT_EDGE",EDGE,{"disambiguationData":[OSD([sQuery(id+"F0.wireOp",EDGE,"E1.bottom"),sQuery(id+"F0.wireOp",EDGE,"E1.right"),sQuery(id+"F0.wireOp",EDGE,"E6")])]});
            chamfer(context, id + "F4", {"entities" : qUnion([Q0, Q1, Q2, Q3, Q4, Q5, Q6, Q7, Q8, Q9, Q10, Q11, Q12, Q13, Q14, Q15, Q16, Q17, Q18, Q19, Q20]), "width" : 0.5 * mm, "tangentPropagation" : true});
        }
    });
